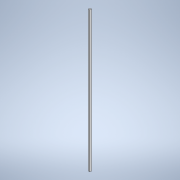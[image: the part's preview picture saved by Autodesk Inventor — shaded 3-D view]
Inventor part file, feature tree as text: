
AUTODESK INVENTOR PART (.ipt)
format: ipt  version: 2022 (Build 260153000, 153)  size: 149,504 bytes
history: native  units: mm
features: extrude x1, sketch x1
ambient origin geometry x8: Origin, YZ Plane, XZ Plane, XY Plane, X Axis, Y Axis, Z Axis, Center Point
bodies: Body1 (feature_tree)
feature tree (2):
  extrude  "Extrusion7"  Depth=5.0mm
  sketch  "Sketch4"  dims[d31=34.456mm d103=5.0mm d104=5.0mm d105=478.0mm d106=0.0mm]
